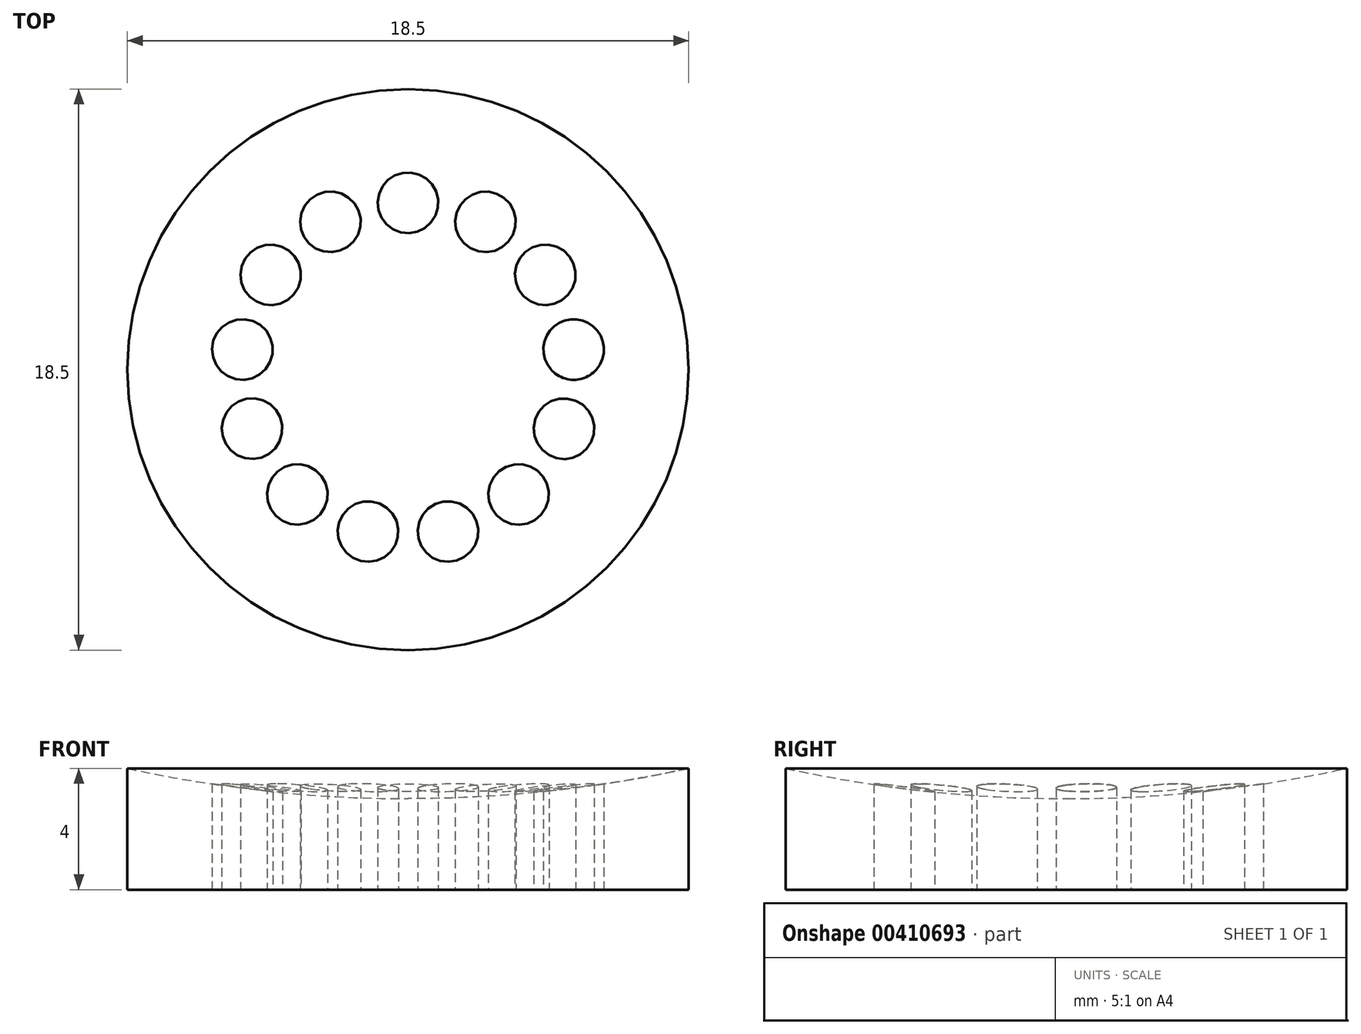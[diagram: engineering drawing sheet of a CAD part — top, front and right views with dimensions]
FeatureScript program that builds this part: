
annotation { "Feature Type Name" : "Feature", "Feature Type Description" : "" }
export const myFeature = defineFeature(function(context is Context, id is Id, definition is map)
    precondition{}
    {
        {
            var Q0;
            Q0=qCreatedBy(makeId("Top.planeOp"),FACE);
            var sketch = newSketch(context, id + "F0", { "sketchPlane" : qUnion([Q0])});
            skCircle(sketch, "E0", {"center": v(0, 0) * mm, "radius": 9.25 * mm});
            skCircle(sketch, "E1", {"center": v(0, 0) * mm, "radius": 5.5 * mm, "construction": true});
            skCircle(sketch, "E2", {"center": v(0, 5.5) * mm, "radius": 1 * mm});
            skCircle(sketch, "E3.1.0", {"center": v(2.56, 4.87) * mm, "radius": 1 * mm});
            skCircle(sketch, "E3.2.0", {"center": v(4.53, 3.12) * mm, "radius": 1 * mm});
            skCircle(sketch, "E3.3.0", {"center": v(5.46, 0.66) * mm, "radius": 1 * mm});
            skCircle(sketch, "E3.4.0", {"center": v(5.14, -1.95) * mm, "radius": 1 * mm});
            skCircle(sketch, "E3.5.0", {"center": v(3.65, -4.12) * mm, "radius": 1 * mm});
            skCircle(sketch, "E3.6.0", {"center": v(1.32, -5.34) * mm, "radius": 1 * mm});
            skCircle(sketch, "E3.7.0", {"center": v(-1.32, -5.34) * mm, "radius": 1 * mm});
            skCircle(sketch, "E3.8.0", {"center": v(-3.65, -4.12) * mm, "radius": 1 * mm});
            skCircle(sketch, "E3.9.0", {"center": v(-5.14, -1.95) * mm, "radius": 1 * mm});
            skCircle(sketch, "E3.10.0", {"center": v(-5.46, 0.66) * mm, "radius": 1 * mm});
            skCircle(sketch, "E3.11.0", {"center": v(-4.53, 3.12) * mm, "radius": 1 * mm});
            skCircle(sketch, "E3.12.0", {"center": v(-2.56, 4.87) * mm, "radius": 1 * mm});
            skLineSegment(sketch, "E3.anchor1", {"start": v(0, 0) * mm, "end": v(0, 5.5) * mm, "construction": true});
            skLineSegment(sketch, "E3.anchor2", {"start": v(0, 0) * mm, "end": v(-2.56, 4.87) * mm, "construction": true});
            skSolve(sketch);
        }
        {
            var Q0;
            Q0=makeQuery(id+"F0.imprint","IMPRINT",FACE,{"disambiguationData":[TD([[makeQuery(id+"F0.imprint","IMPRINT",EDGE,{"derivedFrom":sQuery(id+"F0.wireOp",EDGE,"E0")}),1.0]])]});
            extrude(context, id + "F1", {"entities" : qUnion([Q0]), "depth" : 4 * mm});
        }
        {
            var Q0;
            Q0=qCreatedBy(makeId("Front.planeOp"),FACE);
            var sketch = newSketch(context, id + "F2", { "sketchPlane" : qUnion([Q0])});
            skLineSegment(sketch, "E4.0", {"start": v(0, 4) * mm, "end": v(9.25, 4) * mm});
            skArc(sketch, "E5", {"start": v(0, 3) * mm, "mid": v(4.65, 3.25) * mm, "end": v(9.25, 4) * mm});
            skLineSegment(sketch, "E6", {"start": v(0, 3) * mm, "end": v(0, 4) * mm});
            skPoint(sketch, "E7.orphan", {"position": v(-9.25, 4) * mm});
            skSolve(sketch);
        }
        {
            var Q0;
            Q0 = qSketchRegion(id + "F2", true);
            var Q1;
            Q1=makeQuery(id+"F1.opExtrude","SWEPT_FACE",FACE,{"disambiguationData":[OSD([sQuery(id+"F0.wireOp",EDGE,"E0")])]});
            revolve(context, id + "F3", {"operationType" : NewBodyOperationType.REMOVE, "entities" : qUnion([Q0]), "axis" : qUnion([Q1]), "revolveType" : RevolveType.FULL, "oppositeDirection" : true});
        }
    });
